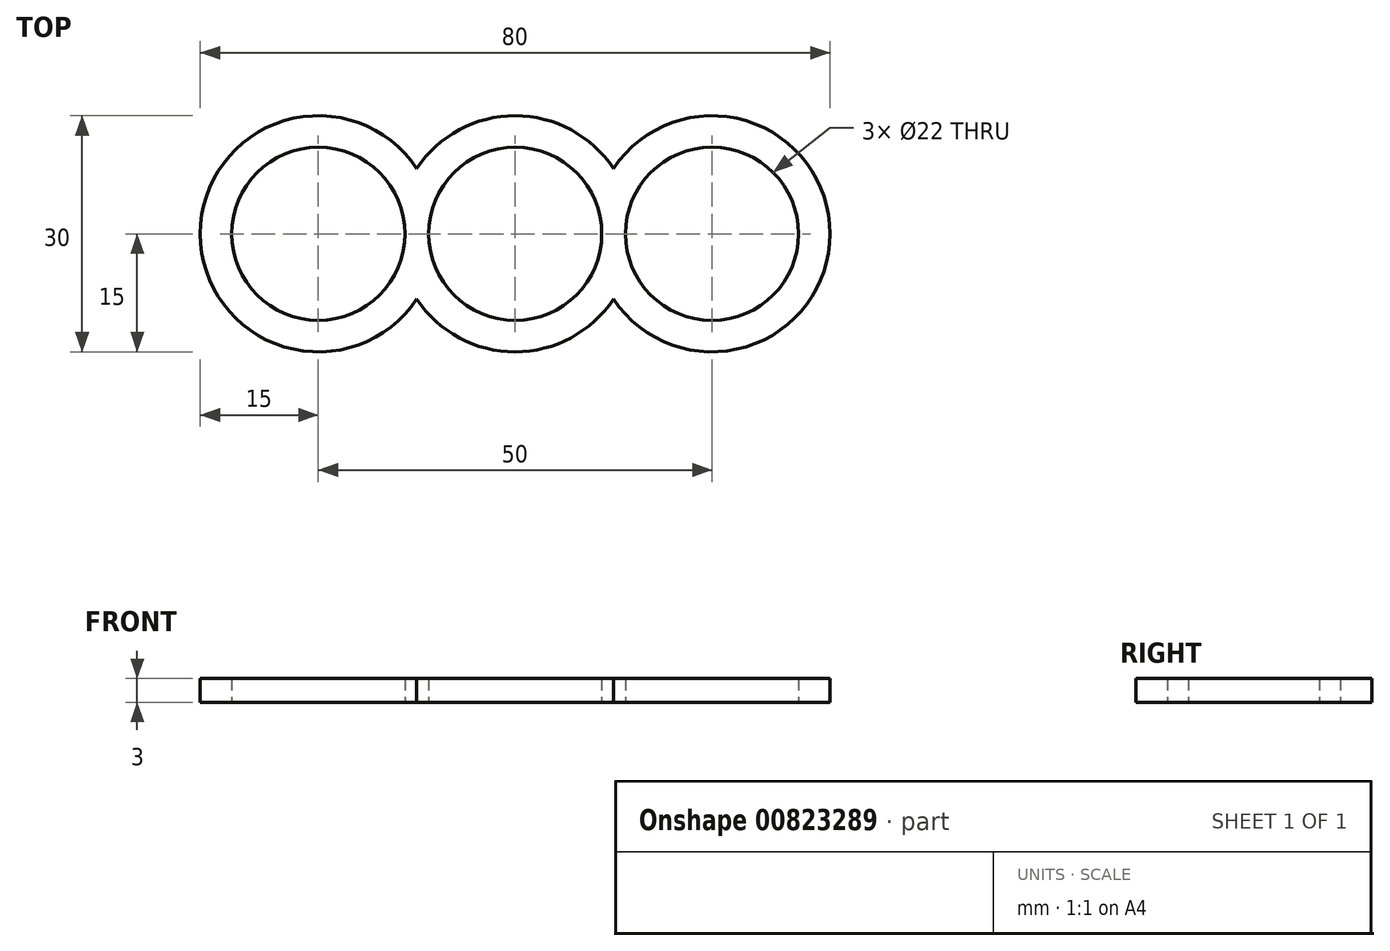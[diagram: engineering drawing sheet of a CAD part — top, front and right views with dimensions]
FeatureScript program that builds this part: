
annotation { "Feature Type Name" : "Feature", "Feature Type Description" : "" }
export const myFeature = defineFeature(function(context is Context, id is Id, definition is map)
    precondition{}
    {
        {
            var Q0;
            Q0=qCreatedBy(makeId("Top.planeOp"),FACE);
            var sketch = newSketch(context, id + "F0", { "sketchPlane" : qUnion([Q0])});
            skArc(sketch, "E0", {"start": v(0, 11) * mm, "mid": v(-11, 0) * mm, "end": v(0, -11) * mm});
            skArc(sketch, "E1", {"start": v(-12.5, -8.3) * mm, "mid": v(-7.1, -13.22) * mm, "end": v(0, -15) * mm});
            skCircle(sketch, "E2", {"center": v(-25, 0) * mm, "radius": 11 * mm});
            skArc(sketch, "E3", {"start": v(-12.5, 8.3) * mm, "mid": v(-40, 0) * mm, "end": v(-12.5, -8.3) * mm});
            skLineSegment(sketch, "E4", {"start": v(0, 15) * mm, "end": v(0, -15) * mm});
            skArc(sketch, "E5.trimOffspring", {"start": v(0, 15) * mm, "mid": v(-7.1, 13.22) * mm, "end": v(-12.5, 8.3) * mm});
            skArc(sketch, "E6.MirrorCS", {"start": v(12.5, -8.3) * mm, "mid": v(7.1, -13.22) * mm, "end": v(0, -15) * mm});
            skArc(sketch, "E7.MirrorCS", {"start": v(0, 15) * mm, "mid": v(7.1, 13.22) * mm, "end": v(12.5, 8.3) * mm});
            skCircle(sketch, "E8.MirrorC", {"center": v(25, 0) * mm, "radius": 11 * mm});
            skArc(sketch, "E9.MirrorCS", {"start": v(12.5, 8.3) * mm, "mid": v(40, 0) * mm, "end": v(12.5, -8.3) * mm});
            skArc(sketch, "E10.MirrorCS", {"start": v(0, 11) * mm, "mid": v(11, 0) * mm, "end": v(0, -11) * mm});
            skSolve(sketch);
        }
        {
            var Q0;
            Q0 = qSketchRegion(id + "F0", true);
            extrude(context, id + "F1", {"entities" : qUnion([Q0]), "depth" : 3 * mm, "offsetDistance" : 25 * mm});
        }
    });
